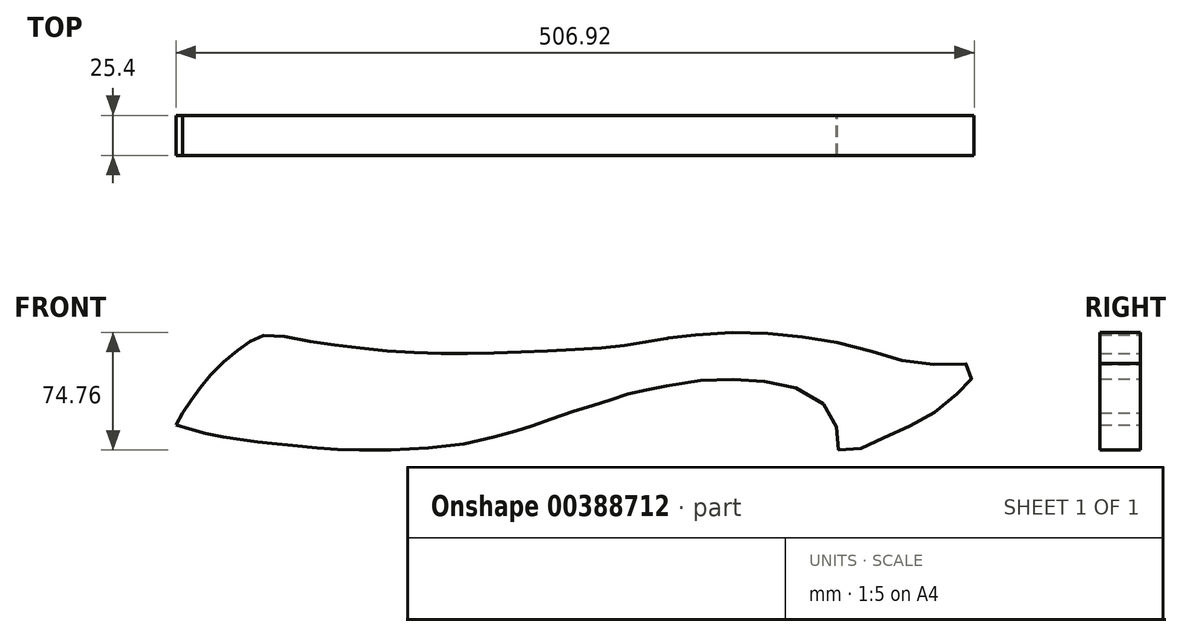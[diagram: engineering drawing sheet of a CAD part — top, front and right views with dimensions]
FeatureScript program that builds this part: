
annotation { "Feature Type Name" : "Feature", "Feature Type Description" : "" }
export const myFeature = defineFeature(function(context is Context, id is Id, definition is map)
    precondition{}
    {
        {
            var Q0;
            Q0=qCreatedBy(makeId("Front.planeOp"),FACE);
            var sketch = newSketch(context, id + "F0", { "sketchPlane" : qUnion([Q0])});
            skLineSegment(sketch, "E0", {"start": v(-42.47, 53.66) * mm, "end": v(-42.47, 10.6) * mm});
            skLineSegment(sketch, "E1", {"start": v(-354.09, -4.17) * mm, "end": v(-354.09, 55.55) * mm});
            skPoint(sketch, "E2", {"position": v(-343.8, 12.48) * mm});
            skPoint(sketch, "E3", {"position": v(-337.3, 21.32) * mm});
            skPoint(sketch, "E4", {"position": v(-327.76, 32.27) * mm});
            skPoint(sketch, "E5", {"position": v(-316.29, 42.52) * mm});
            skPoint(sketch, "E6", {"position": v(-306.74, 49.25) * mm});
            skPoint(sketch, "E7", {"position": v(-297.44, 53.04) * mm});
            skPoint(sketch, "E8", {"position": v(-271.94, 49.54) * mm});
            skPoint(sketch, "E9", {"position": v(-256.1, 53.95) * mm});
            skPoint(sketch, "E10", {"position": v(-242.56, 45.54) * mm});
            skPoint(sketch, "E11", {"position": v(-221.27, 47.78) * mm});
            skPoint(sketch, "E12", {"position": v(-208.88, 42.18) * mm});
            skPoint(sketch, "E13", {"position": v(-187.32, 44.25) * mm});
            skPoint(sketch, "E14", {"position": v(-176.04, 41.33) * mm});
            skPoint(sketch, "E15", {"position": v(-157.77, 43.37) * mm});
            skPoint(sketch, "E16", {"position": v(-142.92, 41.9) * mm});
            skPoint(sketch, "E17", {"position": v(-124.7, 43.81) * mm});
            skPoint(sketch, "E18", {"position": v(-109.14, 43.36) * mm});
            skPoint(sketch, "E19", {"position": v(-89.43, 44.7) * mm});
            skPoint(sketch, "E20", {"position": v(-77.14, 45.6) * mm});
            skPoint(sketch, "E21", {"position": v(-55.48, 48.66) * mm});
            skPoint(sketch, "E22", {"position": v(-349.97, 3.5) * mm});
            skPoint(sketch, "E23", {"position": v(-344.74, -6.9) * mm});
            skPoint(sketch, "E24", {"position": v(-330.18, -10.43) * mm});
            skPoint(sketch, "E25", {"position": v(-315.58, -12.94) * mm});
            skPoint(sketch, "E26", {"position": v(-300.63, -15.04) * mm});
            skPoint(sketch, "E27", {"position": v(-288.84, -16.35) * mm});
            skPoint(sketch, "E28", {"position": v(-261.18, -18.87) * mm});
            skPoint(sketch, "E29", {"position": v(-181.55, -17.55) * mm});
            skPoint(sketch, "E30", {"position": v(-140.22, -8.54) * mm});
            skPoint(sketch, "E31", {"position": v(-126.33, -4.21) * mm});
            skPoint(sketch, "E32", {"position": v(-113.87, 0) * mm});
            skPoint(sketch, "E33", {"position": v(-103.34, 4) * mm});
            skPoint(sketch, "E34", {"position": v(-93.4, 7) * mm});
            skPoint(sketch, "E35", {"position": v(-84.13, 9.87) * mm});
            skPoint(sketch, "E36", {"position": v(-76.86, 12.4) * mm});
            skPoint(sketch, "E37", {"position": v(-68.26, 15.27) * mm});
            skPoint(sketch, "E38", {"position": v(-57.48, 17.57) * mm});
            skPoint(sketch, "E39", {"position": v(-49.87, 19.28) * mm});
            skPoint(sketch, "E40", {"position": v(-42.47, 20.58) * mm});
            skPoint(sketch, "E41", {"position": v(-36.58, 21.84) * mm});
            skPoint(sketch, "E42", {"position": v(-29.35, 22.86) * mm});
            skPoint(sketch, "E43", {"position": v(-22.49, 24.06) * mm});
            skPoint(sketch, "E44", {"position": v(-11.64, 25.02) * mm});
            skPoint(sketch, "E45", {"position": v(-2.74, 25.4) * mm});
            skPoint(sketch, "E46", {"position": v(6.16, 24.65) * mm});
            skPoint(sketch, "E47", {"position": v(14.7, 24.1) * mm});
            skPoint(sketch, "E48", {"position": v(22.85, 23.36) * mm});
            skPoint(sketch, "E49", {"position": v(31.56, 21.5) * mm});
            skPoint(sketch, "E50", {"position": v(40.28, 19.28) * mm});
            skPoint(sketch, "E51", {"position": v(49.34, 15.5) * mm});
            skPoint(sketch, "E52", {"position": v(55.46, 10.6) * mm});
            skPoint(sketch, "E53", {"position": v(59.82, 6.42) * mm});
            skPoint(sketch, "E54", {"position": v(62.88, 1.14) * mm});
            skPoint(sketch, "E55", {"position": v(65, -4.8) * mm});
            skPoint(sketch, "E56", {"position": v(65.94, -10.43) * mm});
            skPoint(sketch, "E57", {"position": v(65.94, -19.46) * mm});
            skPoint(sketch, "E58", {"position": v(-36.58, 51.79) * mm});
            skPoint(sketch, "E59", {"position": v(-25.62, 52.9) * mm});
            skPoint(sketch, "E60", {"position": v(-14.86, 53.64) * mm});
            skPoint(sketch, "E61", {"position": v(-2.74, 54.57) * mm});
            skPoint(sketch, "E62", {"position": v(8.5, 54.57) * mm});
            skPoint(sketch, "E63", {"position": v(18.5, 54.2) * mm});
            skPoint(sketch, "E64", {"position": v(28.15, 52.9) * mm});
            skPoint(sketch, "E65", {"position": v(38.53, 52.53) * mm});
            skPoint(sketch, "E66", {"position": v(48.91, 51.42) * mm});
            skPoint(sketch, "E67", {"position": v(58.92, 49.75) * mm});
            skPoint(sketch, "E68", {"position": v(68.94, 47.34) * mm});
            skPoint(sketch, "E69", {"position": v(80.46, 44.7) * mm});
            skPoint(sketch, "E70", {"position": v(90.03, 41.31) * mm});
            skPoint(sketch, "E71", {"position": v(98.69, 39.1) * mm});
            skPoint(sketch, "E72", {"position": v(106.55, 36.88) * mm});
            skPoint(sketch, "E73", {"position": v(113.24, 35.7) * mm});
            skPoint(sketch, "E74", {"position": v(122.83, 34.65) * mm});
            skPoint(sketch, "E75", {"position": v(132.4, 34.52) * mm});
            skPoint(sketch, "E76", {"position": v(140.4, 34.52) * mm});
            skPoint(sketch, "E77", {"position": v(148.4, 34.65) * mm});
            skPoint(sketch, "E78", {"position": v(152.72, 31.76) * mm});
            skPoint(sketch, "E79", {"position": v(150.36, 24.06) * mm});
            skPoint(sketch, "E80", {"position": v(146.43, 20.58) * mm});
            skPoint(sketch, "E81", {"position": v(142.62, 15.5) * mm});
            skPoint(sketch, "E82", {"position": v(138.3, 12.1) * mm});
            skPoint(sketch, "E83", {"position": v(133.05, 7.9) * mm});
            skPoint(sketch, "E84", {"position": v(73.44, -19.42) * mm});
            skPoint(sketch, "E85", {"position": v(81.83, -18.87) * mm});
            skPoint(sketch, "E86", {"position": v(90.03, -14.57) * mm});
            skPoint(sketch, "E87", {"position": v(95.99, -12.08) * mm});
            skPoint(sketch, "E88", {"position": v(103.59, -8.8) * mm});
            skPoint(sketch, "E89", {"position": v(109.62, -6.05) * mm});
            skPoint(sketch, "E90", {"position": v(115.52, -3.03) * mm});
            skPoint(sketch, "E91", {"position": v(121.42, 0) * mm});
            skPoint(sketch, "E92", {"position": v(127.19, 3.65) * mm});
            skFitSpline(sketch, "E93", {"points": [v(-354.09, -4.17) * mm, v(-344.74, -6.9) * mm, v(-330.18, -10.43) * mm, v(-315.58, -12.94) * mm, v(-300.63, -15.04) * mm, v(-288.84, -16.35) * mm, v(-261.18, -18.87) * mm, v(-240.22, -19.8) * mm, v(-181.55, -17.55) * mm, v(-140.22, -8.54) * mm, v(-126.33, -4.21) * mm, v(-103.34, 4) * mm, v(-84.13, 9.87) * mm, v(-68.26, 15.27) * mm, v(-49.87, 19.28) * mm, v(-29.35, 22.86) * mm, v(-11.64, 25.02) * mm, v(6.16, 24.65) * mm, v(22.85, 23.36) * mm, v(40.28, 19.28) * mm, v(55.46, 10.6) * mm, v(62.88, 1.14) * mm, v(65.94, -10.43) * mm, v(65.94, -19.46) * mm, v(73.44, -19.42) * mm, v(81.83, -18.87) * mm, v(90.03, -14.57) * mm, v(103.59, -8.8) * mm, v(115.52, -3.03) * mm, v(127.19, 3.65) * mm, v(138.3, 12.1) * mm, v(146.43, 20.58) * mm, v(150.36, 24.06) * mm, v(152.72, 31.76) * mm, v(148.4, 34.65) * mm, v(132.4, 34.52) * mm, v(113.24, 35.7) * mm, v(98.69, 39.1) * mm, v(80.46, 44.7) * mm, v(58.92, 49.75) * mm, v(38.53, 52.53) * mm, v(18.5, 54.2) * mm, v(-2.74, 54.57) * mm, v(-25.62, 52.9) * mm, v(-36.58, 51.79) * mm, v(-55.48, 48.66) * mm, v(-77.14, 45.6) * mm, v(-109.14, 43.36) * mm, v(-142.92, 41.9) * mm, v(-176.04, 41.33) * mm, v(-208.88, 42.18) * mm, v(-242.56, 45.54) * mm, v(-271.94, 49.54) * mm, v(-297.44, 53.04) * mm, v(-306.74, 49.25) * mm, v(-316.29, 42.52) * mm, v(-327.76, 32.27) * mm, v(-337.3, 21.32) * mm, v(-343.8, 12.48) * mm, v(-349.97, 3.5) * mm], "startDerivative": vector(742.4, -224.71) * mm, "endDerivative": vector(-430.75, -672.19) * mm});
            skLineSegment(sketch, "E94", {"start": v(-354.09, -4.17) * mm, "end": v(-349.97, 3.5) * mm});
            skLineSegment(sketch, "E95", {"start": v(-41.33, 51.07) * mm, "end": v(-36.58, 21.84) * mm});
            skSolve(sketch);
        }
        {
            var Q0;
            {var subQ0=sQuery(id+"F0.wireOp",EDGE,"E93");var subQ4=makeQuery(id+"F0.imprint","IMPRINT",VERTEX,{"derivedFrom":subQ0});Q0=makeQuery(id+"F0.imprint","IMPRINT",FACE,{"disambiguationData":[TD([[makeQuery(id+"F0.imprint","IMPRINT",EDGE,{"disambiguationData":[TD([[subQ4,1.0]])],"derivedFrom":subQ0}),1.0]])]});}
            var Q1;
            {var subQ4=sQuery(id+"F0.wireOp",EDGE,"E94");Q1=makeQuery(id+"F0.imprint","IMPRINT",FACE,{"disambiguationData":[TD([[makeQuery(id+"F0.imprint","IMPRINT",EDGE,{"derivedFrom":subQ4}),-1.0]])]});}
            extrude(context, id + "F1", {"entities" : qUnion([Q0, Q1]), "depth" : 25.4 * mm});
        }
    });
